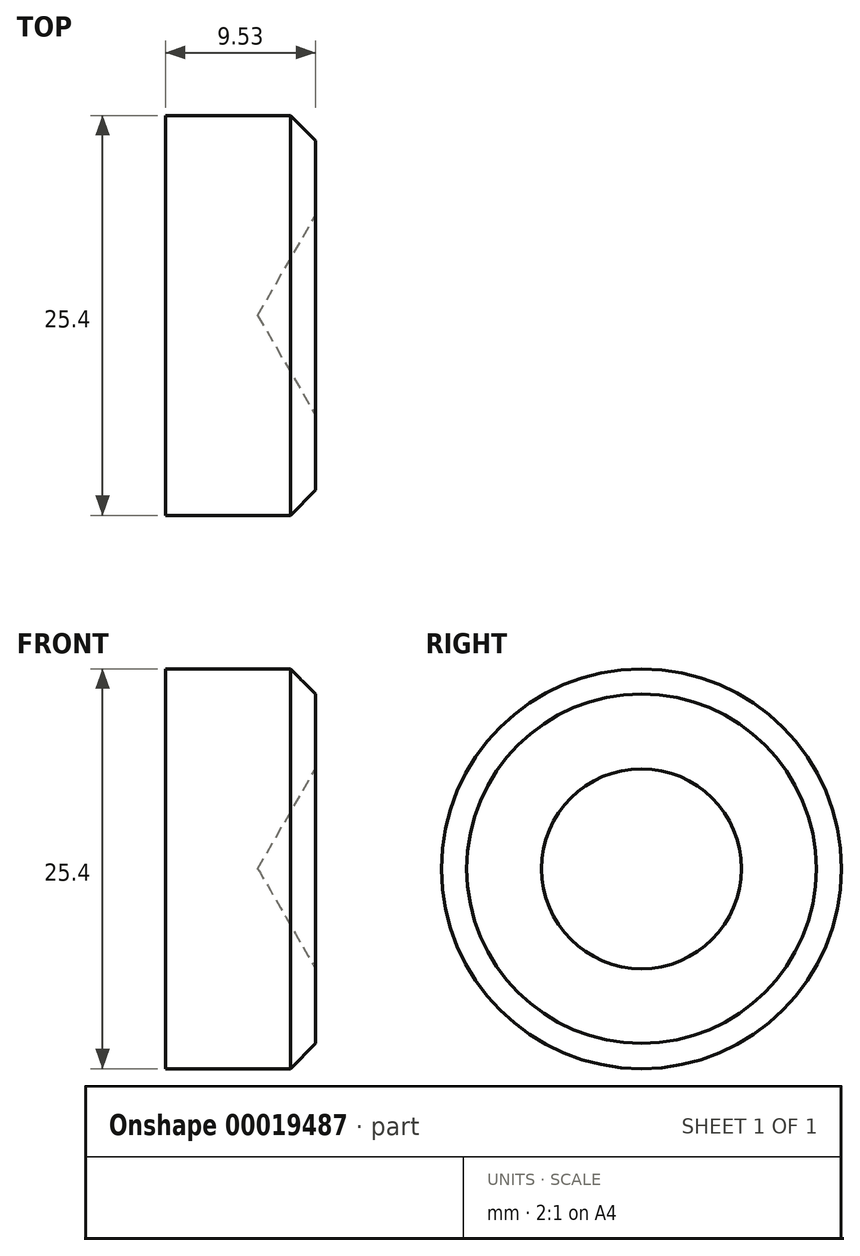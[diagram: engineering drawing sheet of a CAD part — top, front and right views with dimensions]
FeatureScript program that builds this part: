
annotation { "Feature Type Name" : "Feature", "Feature Type Description" : "" }
export const myFeature = defineFeature(function(context is Context, id is Id, definition is map)
    precondition{}
    {
        {
            var Q0;
            Q0=qCreatedBy(makeId("Front.planeOp"),FACE);
            var sketch = newSketch(context, id + "F0", { "sketchPlane" : qUnion([Q0])});
            skLineSegment(sketch, "E0", {"start": v(0, 0) * mm, "end": v(9.53, 0) * mm});
            skLineSegment(sketch, "E1", {"start": v(9.53, 0) * mm, "end": v(9.53, -6.35) * mm});
            skLineSegment(sketch, "E2", {"start": v(9.53, -6.35) * mm, "end": v(5.86, -12.7) * mm});
            skLineSegment(sketch, "E3", {"start": v(5.86, -12.7) * mm, "end": v(0, -12.7) * mm});
            skLineSegment(sketch, "E4", {"start": v(0, -12.7) * mm, "end": v(0, 0) * mm});
            skSolve(sketch);
        }
        {
            var Q0;
            Q0 = qSketchRegion(id + "F0", true);
            var Q1;
            Q1=sQuery(id+"F0.wireOp",EDGE,"E3");
            revolve(context, id + "F1", {"entities" : qUnion([Q0]), "axis" : qUnion([Q1]), "revolveType" : RevolveType.FULL});
        }
        {
            var Q0;
            Q0=makeQuery(id+"F1.opRevolve","SWEPT_EDGE",EDGE,{"disambiguationData":[OSD([sQuery(id+"F0.wireOp",EDGE,"E0"),sQuery(id+"F0.wireOp",EDGE,"E1")])]});
            chamfer(context, id + "F2", {"entities" : qUnion([Q0]), "chamferType" : ChamferType.OFFSET_ANGLE, "width" : 1.6 * mm, "oppositeDirection" : false, "angle" : 45 * degree, "tangentPropagation" : true});
        }
    });
